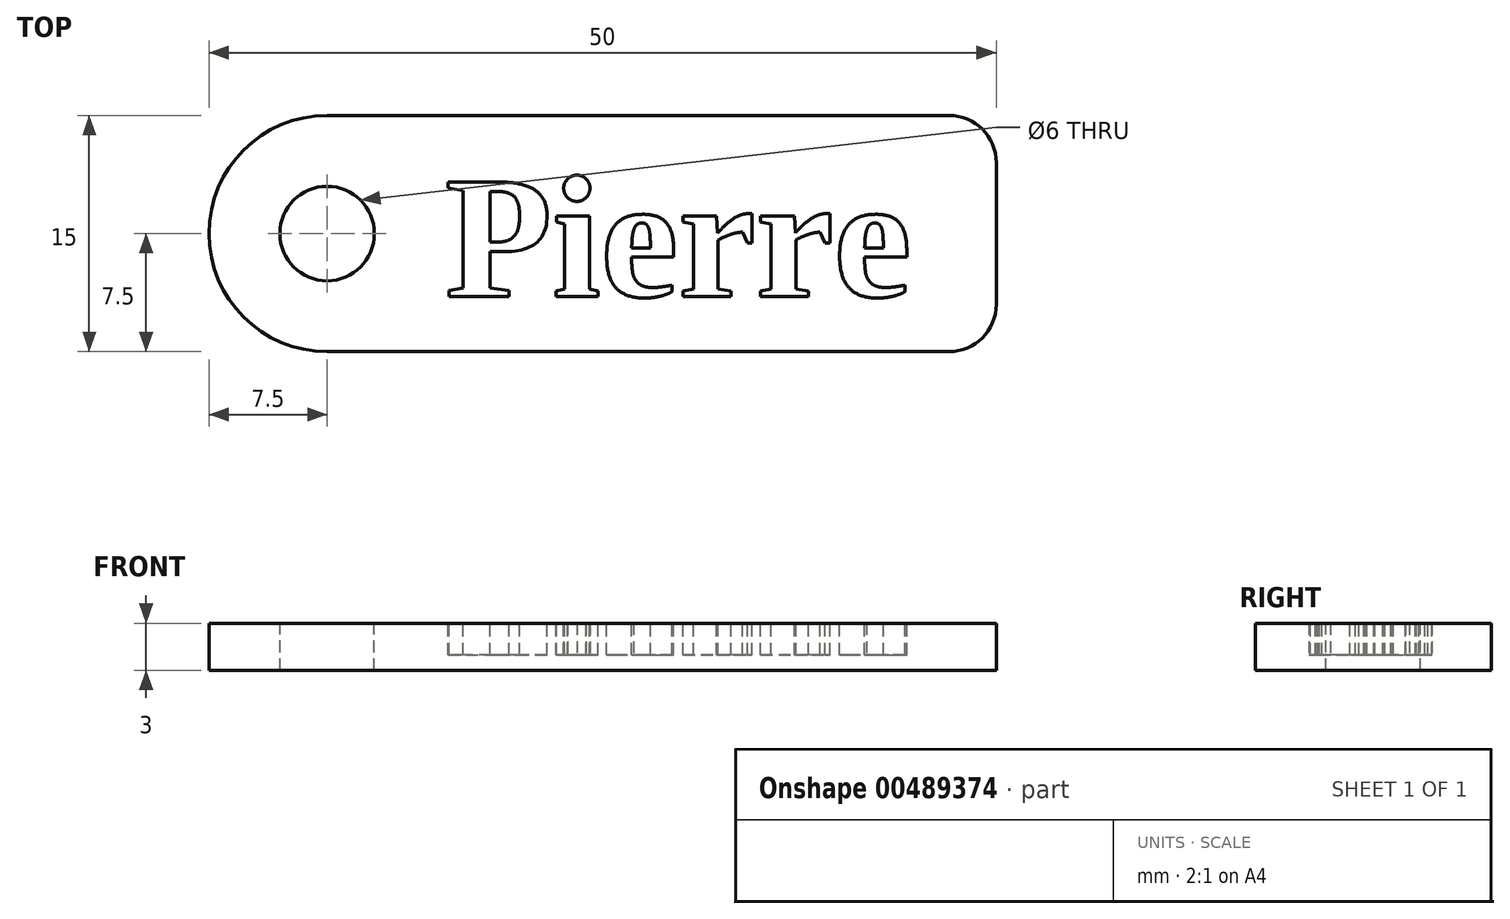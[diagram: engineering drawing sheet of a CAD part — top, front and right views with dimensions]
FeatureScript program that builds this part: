
annotation { "Feature Type Name" : "Feature", "Feature Type Description" : "" }
export const myFeature = defineFeature(function(context is Context, id is Id, definition is map)
    precondition{}
    {
        {
            var Q0;
            Q0=qCreatedBy(makeId("Top.planeOp"),FACE);
            var sketch = newSketch(context, id + "F0", { "sketchPlane" : qUnion([Q0])});
            skLineSegment(sketch, "E0.bottom", {"start": v(0, 0) * mm, "end": v(50, 0) * mm});
            skLineSegment(sketch, "E0.top", {"start": v(0, 15) * mm, "end": v(50, 15) * mm});
            skLineSegment(sketch, "E0.left", {"start": v(0, 0) * mm, "end": v(0, 15) * mm});
            skLineSegment(sketch, "E0.right", {"start": v(50, 0) * mm, "end": v(50, 15) * mm});
            skSolve(sketch);
        }
        {
            var Q0;
            Q0 = qSketchRegion(id + "F0", true);
            var Q1;
            Q1=makeQuery(id+"F0.imprint","IMPRINT",FACE,{"disambiguationData":[TD([[makeQuery(id+"F0.imprint","IMPRINT",EDGE,{"derivedFrom":sQuery(id+"F0.wireOp",EDGE,"E0.bottom")}),1.0]])]});
            extrude(context, id + "F1", {"entities" : qUnion([Q0, Q1]), "depth" : 3 * mm});
        }
        {
            var Q0;
            Q0=makeQuery(id+"F1.opExtrude","CAP_FACE",FACE,{"disambiguationData":[OSD([sQuery(id+"F0.wireOp",EDGE,"E0.bottom"),sQuery(id+"F0.wireOp",EDGE,"E0.top"),sQuery(id+"F0.wireOp",EDGE,"E0.left"),sQuery(id+"F0.wireOp",EDGE,"E0.right")])],"isStart":false});
            var sketch = newSketch(context, id + "F2", { "sketchPlane" : qUnion([Q0])});
            skCircle(sketch, "E1", {"center": v(7.5, 7.5) * mm, "radius": 2.5 * mm});
            skSolve(sketch);
        }
        {
            var Q0;
            Q0=sQuery(id+"F2.wireOp",VERTEX,"E1.center");
            var Q1;
            Q1=makeQuery(id+"F1.opExtrude","SWEPT_BODY",BODY,{"disambiguationData":[OSD([sQuery(id+"F0.wireOp",EDGE,"E0.bottom"),sQuery(id+"F0.wireOp",EDGE,"E0.top"),sQuery(id+"F0.wireOp",EDGE,"E0.left"),sQuery(id+"F0.wireOp",EDGE,"E0.right")])]});
            hole(context, id + "F3", {"style" : HoleStyle.SIMPLE, "endStyle" : HoleEndStyle.THROUGH, "holeDiameter" : 6 * mm, "isTappedThrough" : true, "tappedDepth" : 12 * mm, "tapClearance" : 3, "locations" : qUnion([Q0]), "scope" : qUnion([Q1])});
        }
        {
            var Q0;
            Q0=makeQuery(id+"F1.opExtrude","SWEPT_EDGE",EDGE,{"disambiguationData":[OSD([sQuery(id+"F0.wireOp",EDGE,"E0.top"),sQuery(id+"F0.wireOp",EDGE,"E0.left")])]});
            var Q1;
            Q1=makeQuery(id+"F1.opExtrude","SWEPT_EDGE",EDGE,{"disambiguationData":[OSD([sQuery(id+"F0.wireOp",EDGE,"E0.bottom"),sQuery(id+"F0.wireOp",EDGE,"E0.left")])]});
            fillet(context, id + "F4", {"entities" : qUnion([Q0, Q1]), "radius" : 7.5 * mm, "tangentPropagation" : true, "allowEdgeOverflow" : false});
        }
        {
            var Q0;
            Q0=makeQuery(id+"F1.opExtrude","SWEPT_EDGE",EDGE,{"disambiguationData":[OSD([sQuery(id+"F0.wireOp",EDGE,"E0.top"),sQuery(id+"F0.wireOp",EDGE,"E0.right")])]});
            var Q1;
            Q1=makeQuery(id+"F1.opExtrude","SWEPT_EDGE",EDGE,{"disambiguationData":[OSD([sQuery(id+"F0.wireOp",EDGE,"E0.bottom"),sQuery(id+"F0.wireOp",EDGE,"E0.right")])]});
            fillet(context, id + "F5", {"entities" : qUnion([Q0, Q1]), "radius" : 3 * mm, "tangentPropagation" : true, "allowEdgeOverflow" : false});
        }
        {
            var Q0;
            Q0=makeQuery(id+"F1.opExtrude","CAP_FACE",FACE,{"disambiguationData":[OSD([sQuery(id+"F0.wireOp",EDGE,"E0.bottom"),sQuery(id+"F0.wireOp",EDGE,"E0.top"),sQuery(id+"F0.wireOp",EDGE,"E0.left"),sQuery(id+"F0.wireOp",EDGE,"E0.right")])],"isStart":false});
            var sketch = newSketch(context, id + "F6", { "sketchPlane" : qUnion([Q0])});
            skText(sketch, "E2", { "text": "Pierre", "fontName": "Tinos-Bold.ttf"});
            const initialGuessF6  = {"E2": [0.015, 0.0035, 1, 0, 0.008]};
            skSetInitialGuess(sketch, initialGuessF6);
            skSolve(sketch);
        }
        {
            var Q0;
            Q0 = qSketchRegion(id + "F6", true);
            extrude(context, id + "F7", {"entities" : qUnion([Q0]), "operationType" : NewBodyOperationType.REMOVE, "oppositeDirection" : true, "depth" : 2 * mm});
        }
    });
